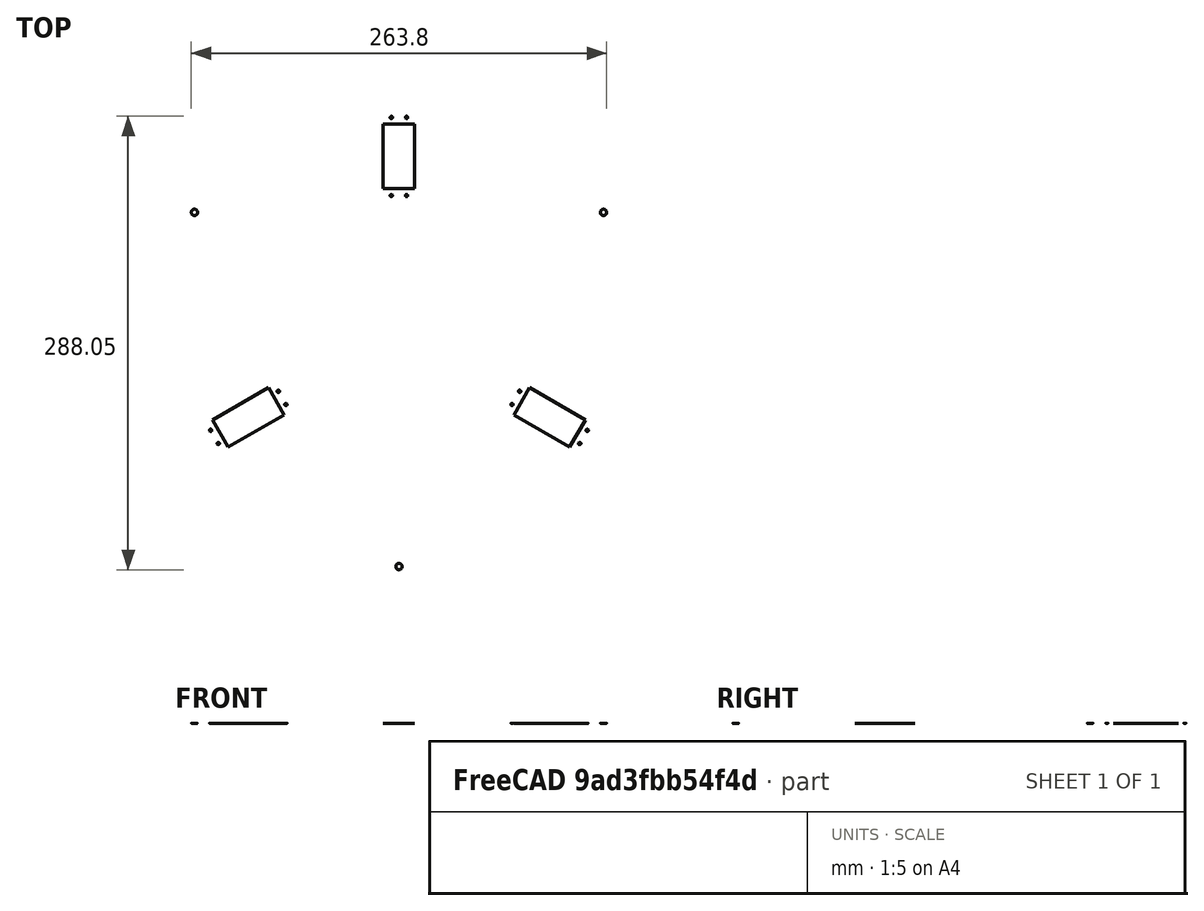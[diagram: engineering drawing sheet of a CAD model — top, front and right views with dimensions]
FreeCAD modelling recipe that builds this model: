
FCSTD DOCUMENT  (FreeCAD 0.16RUnknown)
Label: cylinderServoFace
License: All rights reserved
LicenseURL: http://en.wikipedia.org/wiki/All_rights_reserved
objects: Part::FeaturePython×11, Part::Part2DObjectPython×10, Spreadsheet::Sheet×1
note: 21 computed .brp shape members not serialized (recipe doc carries the construction recipe); baked Part::Feature solids carry a one-line shape summary decoded from their .brp

FEATURE [Part::Part2DObjectPython] Circle  label="circleExternal"  # Draft 2D object (typed FeaturePython)
  FirstAngle = 0
  LastAngle = 360
  MakeFace = true
  Radius = 160
  expr: Radius = prefs.circleExternal / 2
FEATURE [Part::Part2DObjectPython] Rectangle  label="servo"  # Draft 2D object (typed FeaturePython)
  ChamferSize = 0
  Columns = 1
  FilletRadius = 0
  Height = 41
  Length = 20
  MakeFace = true
  Placement = pos=(-10,90,0) rot=(0,0,1;0rad)
  Rows = 1
  expr: Placement.Base.y = prefs.servoDistance
  expr: Height = prefs.servoLength
FEATURE [Part::FeaturePython] Array  label="servoArray"  # Draft array (typed FeaturePython)
  Angle = 360
  ArrayType = 1
  Axis = (0,0,1)
  Base = -> Rectangle
  Center = (0,0,0)
  Fuse = false
  IntervalAxis = (0,0,0)
  IntervalX = (1,0,0)
  IntervalY = (0,1,0)
  IntervalZ = (0,0,0)
  NumberPolar = 3
  NumberX = 1
  NumberY = 1
  NumberZ = 1
  expr: NumberPolar = prefs.servoNumber
FEATURE [Part::Part2DObjectPython] Circle002  label="screw"  # Draft 2D object (typed FeaturePython)
  FirstAngle = 0
  LastAngle = 0
  MakeFace = true
  Placement = pos=(0,150,0) rot=(0,0,1;0rad)
  Radius = 2
  expr: Radius = prefs.screwDiameter / 2
  expr: Placement.Base.x = 0
  expr: Placement.Base.y = prefs.circleExternal / 2 - 10
FEATURE [Part::FeaturePython] Array001  label="screwArray"  # Draft array (typed FeaturePython)
  Angle = 360
  ArrayType = 1
  Axis = (0,0,1)
  Base = -> Circle002
  Center = (0,0,0)
  Fuse = false
  IntervalAxis = (0,0,0)
  IntervalX = (1,0,0)
  IntervalY = (0,1,0)
  IntervalZ = (0,0,0)
  NumberPolar = 3
  NumberX = 1
  NumberY = 1
  NumberZ = 1
  Placement = pos=(0,0,0) rot=(0,0,1;1.0472rad)
  expr: Placement.Rotation.Angle = 180 / prefs.servoNumber
  expr: NumberPolar = prefs.servoNumber
FEATURE [Spreadsheet::Sheet] Spreadsheet  label="prefs"
  cells = A2=External circle diameter; B2(circleExternal)=320; C2=mm; D2=name = circleExternal; A3=Internal circle diameter; B3(circleInternal)=178; C3=mm; D3=name = circleInternal; A4=Number of servo; B4(servoNumber)=3; C4=mm; D4=name = servoNumber; A5=Diameter screw; B5(screwDiameter)=4; C5=mm; D5=name = ; A6=Servo width ; B6(servoWidth)=20; C6=mm; D6=name = servoWidth; A7=Servo length; B7(servoLength)=41; C7=mm; D7=name = servoLength; A8=Smaller distance from servo border to rotation axis; B8(borderAxisDistance)=10; C8=mm; D8=name = borderAxisDistance; A9=Diameter servo fixation hole; B9(servoHole)=1.5; C9=mm; D9=name = servoHole; A10=Servo distance to center; B10(servoDistance)=90; C10=mm; D10=name = servoDistance
FEATURE [Part::Part2DObjectPython] Circle003  # Draft 2D object (typed FeaturePython)
  FirstAngle = 0
  LastAngle = 0
  MakeFace = true
  Radius = 35
FEATURE [Part::FeaturePython] Array002  label="arcArray"  # Draft array (typed FeaturePython)
  Angle = 360
  ArrayType = 1
  Axis = (0,0,1)
  Center = (0,0,0)
  Fuse = false
  IntervalAxis = (0,0,0)
  IntervalX = (1,0,0)
  IntervalY = (0,1,0)
  IntervalZ = (0,0,0)
  NumberPolar = 3
  NumberX = 1
  NumberY = 1
  NumberZ = 1
FEATURE [Part::Part2DObjectPython] Line  # Draft 2D object (typed FeaturePython)
  Closed = false
  Degree = 1
  MakeFace = true
  Points = (2) [(24.9494,117.378,0),(24.9494,117.378,0)]
FEATURE [Part::FeaturePython] Point  # WARN: FeaturePython — macro-defined, semantics opaque (R4)
  X = 0
  Y = 0
  Z = 0
FEATURE [Part::FeaturePython] Point001  # WARN: FeaturePython — macro-defined, semantics opaque (R4)
  X = 0
  Y = 99
  Z = 0
FEATURE [Part::Part2DObjectPython] Arc  # Draft 2D object (typed FeaturePython)
  FirstAngle = -18.49
  LastAngle = 78.49
  MakeFace = true
  Radius = 125
FEATURE [Part::FeaturePython] Array004  label="arcArray001"  # Draft array (typed FeaturePython)
  Angle = 360
  ArrayType = 1
  Axis = (0,0,1)
  Base = -> Arc
  Center = (0,0,0)
  Fuse = false
  IntervalAxis = (0,0,0)
  IntervalX = (1,0,0)
  IntervalY = (0,1,0)
  IntervalZ = (0,0,0)
  NumberPolar = 3
  NumberX = 1
  NumberY = 1
  NumberZ = 1
FEATURE [Part::Part2DObjectPython] Line001  # Draft 2D object (typed FeaturePython)
  ChamferSize = 0
  Closed = false
  End = (-24.9424,77.6874,0)
  FilletRadius = 0
  Length = 44.7988
  MakeFace = true
  Points = (2) [(-24.9424,122.486,0),(-24.9424,77.6874,0)]
  Start = (-24.9424,122.486,0)
  Subdivisions = 0
FEATURE [Part::Part2DObjectPython] Line002  # Draft 2D object (typed FeaturePython)
  ChamferSize = 0
  Closed = false
  End = (24.9424,77.6874,0)
  FilletRadius = 0
  Length = 44.7988
  MakeFace = true
  Points = (2) [(24.9424,122.486,0),(24.9424,77.6874,0)]
  Start = (24.9424,122.486,0)
  Subdivisions = 0
FEATURE [Part::Part2DObjectPython] Line003  # Draft 2D object (typed FeaturePython)
  ChamferSize = 0
  Closed = false
  End = (24.9424,77.6874,0)
  FilletRadius = 0
  Length = 49.8847
  MakeFace = true
  Points = (2) [(-24.9424,77.6874,0),(24.9424,77.6874,0)]
  Start = (-24.9424,77.6874,0)
  Subdivisions = 0
FEATURE [Part::FeaturePython] Array005  label="side1Array"  # Draft array (typed FeaturePython)
  Angle = 360
  ArrayType = 1
  Axis = (0,0,1)
  Base = -> Line001
  Center = (0,0,0)
  Fuse = false
  IntervalAxis = (0,0,0)
  IntervalX = (1,0,0)
  IntervalY = (0,1,0)
  IntervalZ = (0,0,0)
  NumberPolar = 3
  NumberX = 1
  NumberY = 1
  NumberZ = 1
FEATURE [Part::FeaturePython] Array006  label="side2Array"  # Draft array (typed FeaturePython)
  Angle = 360
  ArrayType = 1
  Axis = (0,0,1)
  Base = -> Line003
  Center = (0,0,0)
  Fuse = false
  IntervalAxis = (0,0,0)
  IntervalX = (1,0,0)
  IntervalY = (0,1,0)
  IntervalZ = (0,0,0)
  NumberPolar = 3
  NumberX = 1
  NumberY = 1
  NumberZ = 1
FEATURE [Part::FeaturePython] Array007  label="side3Array"  # Draft array (typed FeaturePython)
  Angle = 360
  ArrayType = 1
  Axis = (0,0,1)
  Base = -> Line002
  Center = (0,0,0)
  Fuse = false
  IntervalAxis = (0,0,0)
  IntervalX = (1,0,0)
  IntervalY = (0,1,0)
  IntervalZ = (0,0,0)
  NumberPolar = 3
  NumberX = 1
  NumberY = 1
  NumberZ = 1
  expr: NumberPolar = prefs.servoNumber
FEATURE [Part::Part2DObjectPython] Circle004  label="servoHole"  # Draft 2D object (typed FeaturePython)
  FirstAngle = 0
  LastAngle = 0
  MakeFace = true
  Placement = pos=(-4.85,85.7,0) rot=(0,0,1;0rad)
  Radius = 0.75
  Support = -> Array
  expr: Placement.Base.y = prefs.servoDistance - 4.3
  expr: Placement.Base.x = -5.5 / 2 - 2.1
  expr: Radius = prefs.servoHole / 2
FEATURE [Part::FeaturePython] Array008  label="servoHoleArray"  # Draft array (typed FeaturePython)
  Angle = 360
  ArrayType = 0
  Axis = (0,0,1)
  Base = -> Circle004
  Center = (0,0,0)
  Fuse = false
  IntervalAxis = (0,0,0)
  IntervalX = (9.7,0,0)
  IntervalY = (0,49.6,0)
  IntervalZ = (0,0,0)
  NumberPolar = 1
  NumberX = 2
  NumberY = 2
  NumberZ = 1
  expr: IntervalY.y = prefs.servoLength + 2 * 4.3
FEATURE [Part::FeaturePython] Array009  label="arrayOfHoleServo"  # Draft array (typed FeaturePython)
  Angle = 360
  ArrayType = 1
  Axis = (0,0,1)
  Base = -> Array008
  Center = (0,0,0)
  Fuse = false
  IntervalAxis = (0,0,0)
  IntervalX = (1,0,0)
  IntervalY = (0,1,0)
  IntervalZ = (0,0,0)
  NumberPolar = 3
  NumberX = 1
  NumberY = 1
  NumberZ = 1
  expr: NumberPolar = prefs.servoNumber
